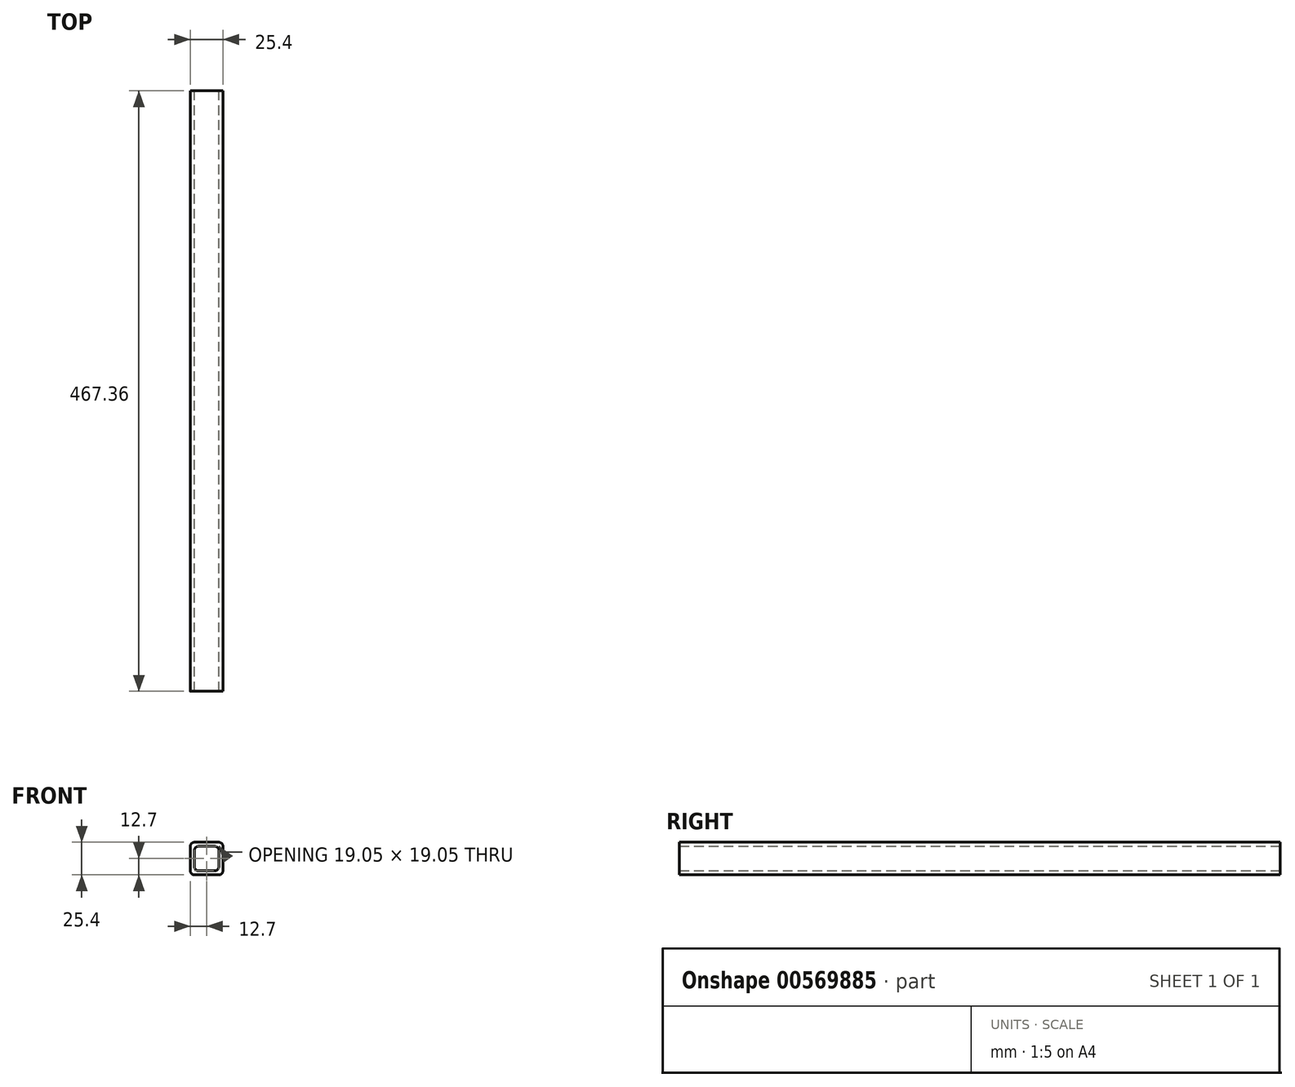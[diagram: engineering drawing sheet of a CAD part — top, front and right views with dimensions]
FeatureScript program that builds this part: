
annotation { "Feature Type Name" : "Feature", "Feature Type Description" : "" }
export const myFeature = defineFeature(function(context is Context, id is Id, definition is map)
    precondition{}
    {
        {
            var Q0;
            Q0=qCreatedBy(makeId("Front.planeOp"),FACE);
            var sketch = newSketch(context, id + "F0", { "sketchPlane" : qUnion([Q0])});
            skLineSegment(sketch, "E0.bottom", {"start": v(9.53, -12.7) * mm, "end": v(-9.52, -12.7) * mm});
            skLineSegment(sketch, "E0.top", {"start": v(9.53, 12.7) * mm, "end": v(-9.53, 12.7) * mm});
            skLineSegment(sketch, "E0.left", {"start": v(12.7, -9.53) * mm, "end": v(12.7, 9.53) * mm});
            skLineSegment(sketch, "E0.right", {"start": v(-12.7, -9.53) * mm, "end": v(-12.7, 9.52) * mm});
            skLineSegment(sketch, "E1.bottom", {"start": v(6.35, -9.52) * mm, "end": v(-6.35, -9.53) * mm});
            skLineSegment(sketch, "E1.top", {"start": v(6.35, 9.53) * mm, "end": v(-6.35, 9.52) * mm});
            skLineSegment(sketch, "E1.left", {"start": v(9.52, -6.35) * mm, "end": v(9.52, 6.35) * mm});
            skLineSegment(sketch, "E1.right", {"start": v(-9.52, -6.35) * mm, "end": v(-9.53, 6.35) * mm});
            skPoint(sketch, "E2.visualSharp", {"position": v(9.52, 9.53) * mm});
            skArc(sketch, "E2.filletArc", {"start": v(9.53, 6.35) * mm, "mid": v(8.6, 8.6) * mm, "end": v(6.35, 9.53) * mm});
            skPoint(sketch, "E3.visualSharp", {"position": v(-9.53, 9.53) * mm});
            skArc(sketch, "E3.filletArc", {"start": v(-6.35, 9.53) * mm, "mid": v(-8.6, 8.6) * mm, "end": v(-9.53, 6.35) * mm});
            skPoint(sketch, "E4.visualSharp", {"position": v(-9.52, -9.53) * mm});
            skArc(sketch, "E4.filletArc", {"start": v(-9.52, -6.35) * mm, "mid": v(-8.6, -8.6) * mm, "end": v(-6.35, -9.53) * mm});
            skPoint(sketch, "E5.visualSharp", {"position": v(9.53, -9.52) * mm});
            skArc(sketch, "E5.filletArc", {"start": v(6.35, -9.52) * mm, "mid": v(8.6, -8.6) * mm, "end": v(9.52, -6.35) * mm});
            skPoint(sketch, "E6.visualSharp", {"position": v(12.7, 12.7) * mm});
            skArc(sketch, "E6.filletArc", {"start": v(12.7, 9.53) * mm, "mid": v(11.77, 11.77) * mm, "end": v(9.53, 12.7) * mm});
            skPoint(sketch, "E7.visualSharp", {"position": v(-12.7, 12.7) * mm});
            skArc(sketch, "E7.filletArc", {"start": v(-9.53, 12.7) * mm, "mid": v(-11.77, 11.77) * mm, "end": v(-12.7, 9.52) * mm});
            skPoint(sketch, "E8.visualSharp", {"position": v(-12.7, -12.7) * mm});
            skArc(sketch, "E8.filletArc", {"start": v(-12.7, -9.53) * mm, "mid": v(-11.77, -11.77) * mm, "end": v(-9.52, -12.7) * mm});
            skPoint(sketch, "E9.visualSharp", {"position": v(12.7, -12.7) * mm});
            skArc(sketch, "E9.filletArc", {"start": v(9.53, -12.7) * mm, "mid": v(11.77, -11.77) * mm, "end": v(12.7, -9.53) * mm});
            skSolve(sketch);
        }
        {
            var Q0;
            Q0 = qSketchRegion(id + "F0", true);
            extrude(context, id + "F1", {"entities" : qUnion([Q0]), "depth" : 467.36 * mm, "offsetDistance" : 25.4 * mm});
        }
    });
